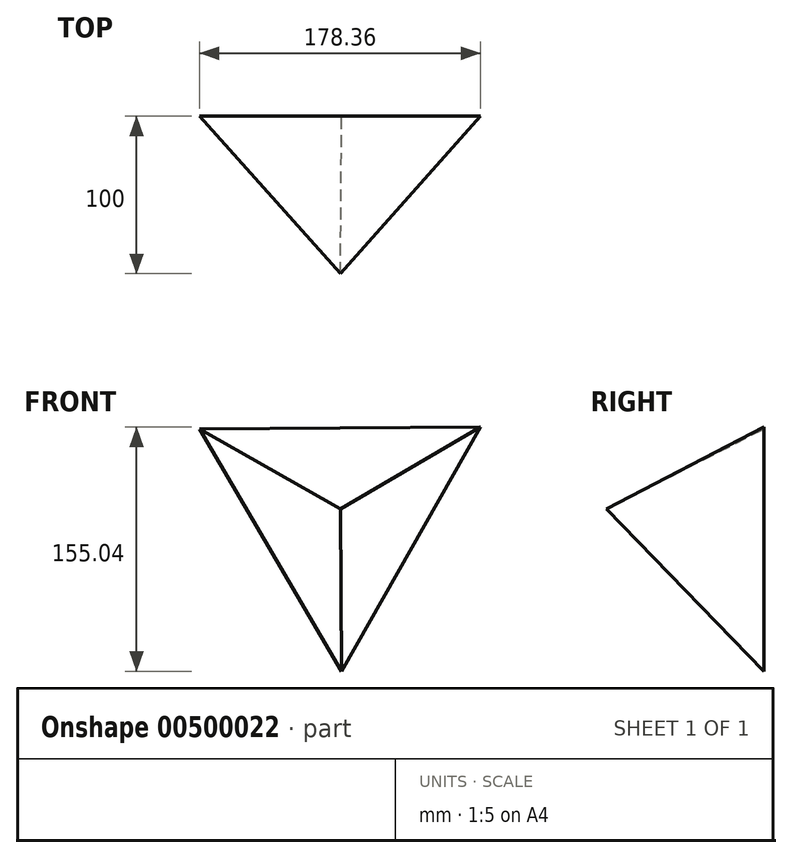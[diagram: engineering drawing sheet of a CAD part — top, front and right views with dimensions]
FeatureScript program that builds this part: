
annotation { "Feature Type Name" : "Feature", "Feature Type Description" : "" }
export const myFeature = defineFeature(function(context is Context, id is Id, definition is map)
    precondition{}
    {
        {
            var Q0;
            Q0=qCreatedBy(makeId("Front.planeOp"),FACE);
            var sketch = newSketch(context, id + "F0", { "sketchPlane" : qUnion([Q0])});
            skCircle(sketch, "E0.cCircle", {"center": v(0, 0) * mm, "radius": 102.98 * mm, "construction": true});
            skLineSegment(sketch, "E0.0", {"start": v(-89.5, 50.92) * mm, "end": v(88.85, 52.06) * mm});
            skLineSegment(sketch, "E0.1", {"start": v(88.85, 52.06) * mm, "end": v(0.65, -102.98) * mm});
            skLineSegment(sketch, "E0.2", {"start": v(0.65, -102.98) * mm, "end": v(-89.5, 50.92) * mm});
            skSolve(sketch);
        }
        {
            var Q0;
            Q0=qCreatedBy(makeId("Front.planeOp"),FACE);
            cPlane(context, id + "F1", {"entities" : qUnion([Q0]), "cplaneType" : CPlaneType.OFFSET, "offset" : 100 * mm, "width" : 150 * mm, "height" : 150 * mm});
        }
        {
            var Q0;
            Q0=qCreatedBy(id+"F1.planeOp",FACE);
            var sketch = newSketch(context, id + "F2", { "sketchPlane" : qUnion([Q0])});
            skPoint(sketch, "E1", {"position": v(-15.19, -8.03) * mm});
            skPoint(sketch, "E2", {"position": v(0, 0) * mm});
            skSolve(sketch);
        }
        {
            var Q0;
            Q0=sQuery(id+"F2.wireOp",VERTEX,"E2");
            var Q1;
            Q1=makeQuery(id+"F0.imprint","IMPRINT",FACE,{"disambiguationData":[TD([[makeQuery(id+"F0.imprint","IMPRINT",EDGE,{"derivedFrom":sQuery(id+"F0.wireOp",EDGE,"E0.0")}),-1.0]])]});
            loft(context, id + "F3", {"sheetProfilesArray" : [{ "sheetProfileEntities" : qUnion([Q0]) }, { "sheetProfileEntities" : qUnion([Q1]) }]});
        }
    });
